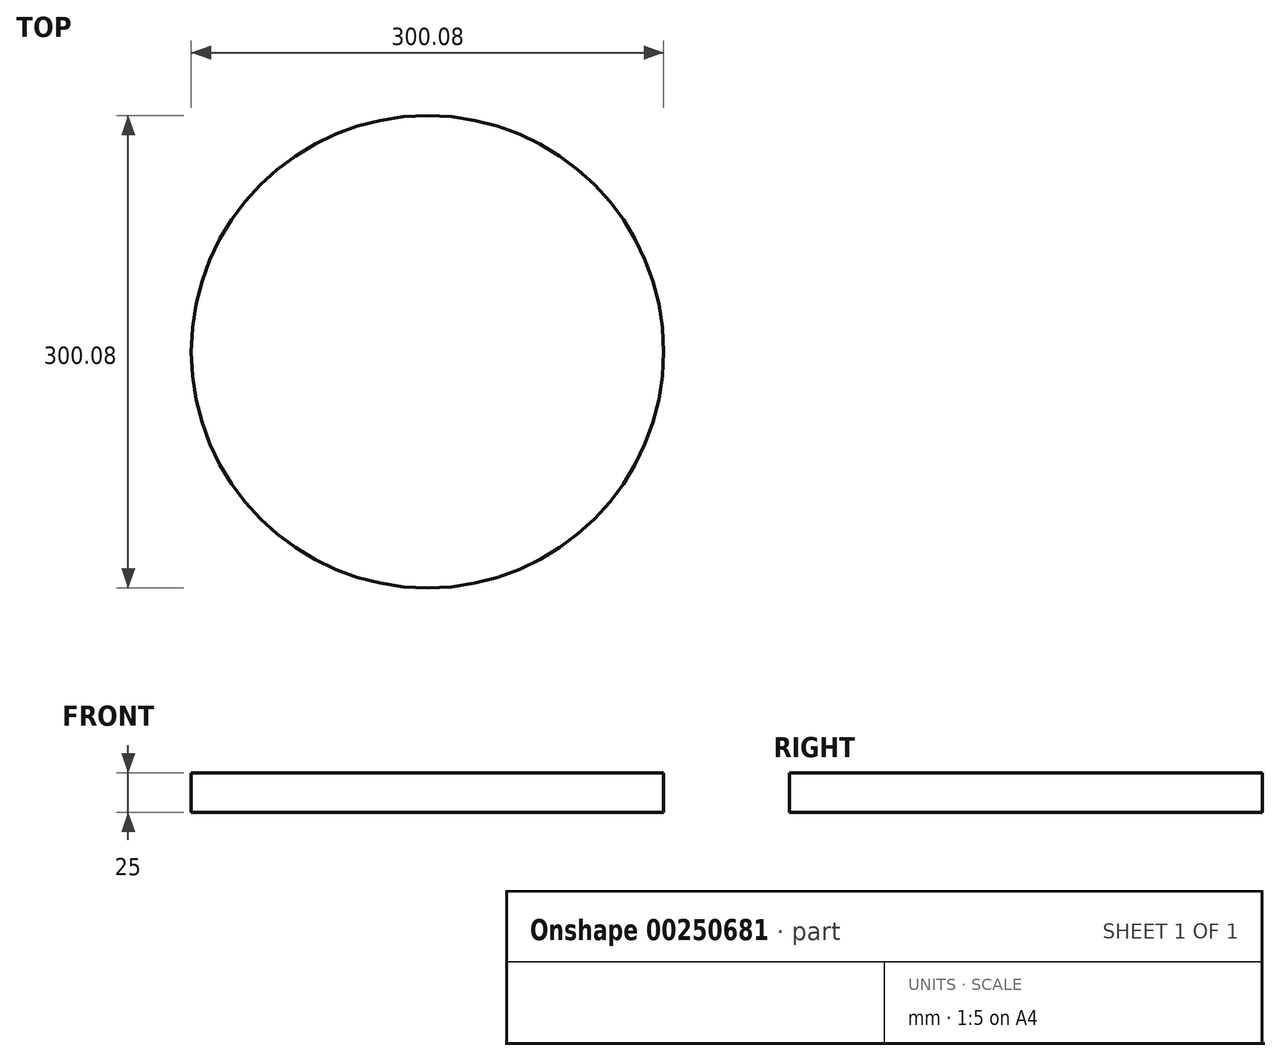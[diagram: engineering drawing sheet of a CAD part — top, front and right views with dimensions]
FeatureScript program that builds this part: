
annotation { "Feature Type Name" : "Feature", "Feature Type Description" : "" }
export const myFeature = defineFeature(function(context is Context, id is Id, definition is map)
    precondition{}
    {
        {
            var Q0;
            Q0=qCreatedBy(makeId("Top.planeOp"),FACE);
            var sketch = newSketch(context, id + "F0", { "sketchPlane" : qUnion([Q0])});
            skCircle(sketch, "E0", {"center": v(0, 0) * mm, "radius": 150.04 * mm});
            skSolve(sketch);
        }
        {
            var Q0;
            Q0=sQuery(id+"F0.wireOp",EDGE,"E0");
            extrude(context, id + "F1", {"bodyType" : ToolBodyType.SURFACE, "surfaceEntities" : qUnion([Q0]), "depth" : 25 * mm});
        }
    });
